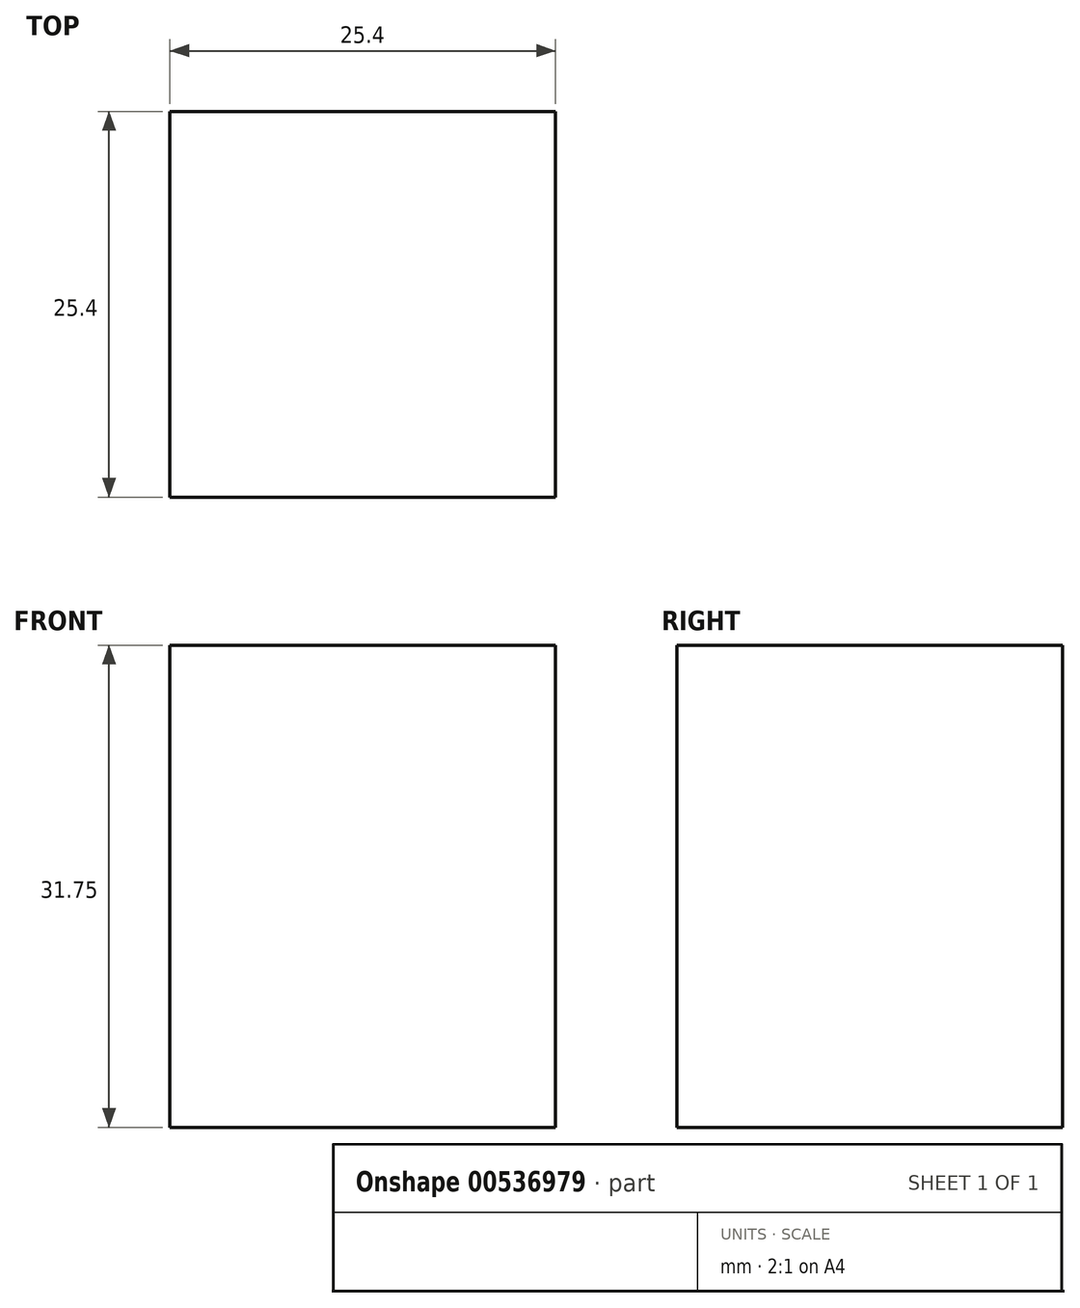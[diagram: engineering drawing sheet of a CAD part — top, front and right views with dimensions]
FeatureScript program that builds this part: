
annotation { "Feature Type Name" : "Feature", "Feature Type Description" : "" }
export const myFeature = defineFeature(function(context is Context, id is Id, definition is map)
    precondition{}
    {
        {
            var Q0;
            Q0=qCreatedBy(makeId("Front.planeOp"),FACE);
            var sketch = newSketch(context, id + "F0", { "sketchPlane" : qUnion([Q0])});
            skLineSegment(sketch, "E0", {"start": v(-51.19, 16.2) * mm, "end": v(-25.79, 16.2) * mm});
            skLineSegment(sketch, "E1", {"start": v(-51.19, 16.2) * mm, "end": v(-51.19, 47.95) * mm});
            skLineSegment(sketch, "E2", {"start": v(-51.19, 47.95) * mm, "end": v(-25.79, 47.95) * mm});
            skLineSegment(sketch, "E3", {"start": v(-25.79, 47.95) * mm, "end": v(-25.79, 16.2) * mm});
            skSolve(sketch);
        }
        {
            var Q0;
            Q0=makeQuery(id+"F0.imprint","IMPRINT",FACE,{"disambiguationData":[TD([[makeQuery(id+"F0.imprint","IMPRINT",EDGE,{"derivedFrom":sQuery(id+"F0.wireOp",EDGE,"E0")}),1.0]])]});
            extrude(context, id + "F1", {"entities" : qUnion([Q0]), "depth" : 25.4 * mm, "offsetDistance" : 25.4 * mm});
        }
    });
